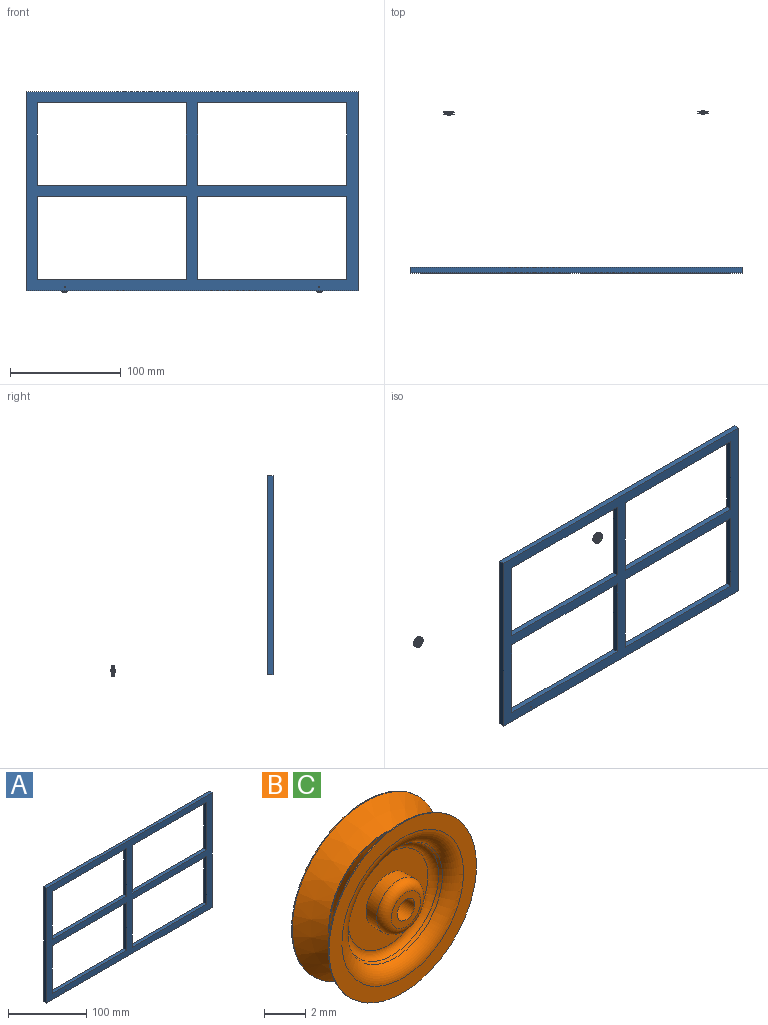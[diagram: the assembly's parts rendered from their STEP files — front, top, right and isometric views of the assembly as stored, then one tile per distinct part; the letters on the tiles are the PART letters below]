
ASSEMBLY  parts=3 mates=2
PART A: 24 faces, bbox 300x5x180 mm
  f0: plane 135x5mm, normal (0,0,-1), area 675mm2, adj f13,f14,f15,f16
  f1: plane 75x5mm, normal (-1,0,0), area 375mm2, adj f6,f14,f15,f21
  f2: plane 135x5mm, normal (0,0,1), area 675mm2, adj f3,f14,f15,f19
  f3: plane 75x5mm, normal (1,0,0), area 375mm2, adj f2,f14,f15,f18
  f4: plane 135x5mm, normal (0,0,-1), area 675mm2, adj f5,f14,f15,f23
  f5: plane 75x5mm, normal (-1,0,0), area 375mm2, adj f4,f14,f15,f22
  f6: plane 135x5mm, normal (0,0,1), area 675mm2, adj f1,f14,f15,f20
  f7: plane 180x5mm, normal (-1,0,0), area 900mm2, adj f8,f12,f14,f15
  f8: plane 300x5mm, normal (0,0,-1), area 1500mm2, adj f7,f9,f14,f15
  f9: plane 180x5mm, normal (1,0,0), area 900mm2, adj f8,f12,f14,f15
  f10: cylinder r=0.6mm len=5mm, axis (0,1,0), area 18.8mm2, adj f14,f15
  f11: cylinder r=0.6mm len=5mm, axis (0,1,0), area 18.8mm2, adj f14,f15
  f12: plane 300x5mm, normal (0,0,1), area 1500mm2, adj f7,f9,f14,f15
  f13: plane 75x5mm, normal (1,0,0), area 375mm2, adj f0,f14,f15,f17
  f14: plane 300x180mm, normal (0,-1,0), area 13497.7mm2, adj f0,f1,f2,f3,f4,f5,f6,f7
  f15: plane 300x180mm, normal (0,1,0), area 13497.7mm2, adj f0,f1,f2,f3,f4,f5,f6,f7
  f16: plane 75x5mm, normal (-1,0,0), area 375mm2, adj f0,f14,f15,f17
  f17: plane 135x5mm, normal (0,0,1), area 675mm2, adj f13,f14,f15,f16
  f18: plane 135x5mm, normal (0,0,-1), area 675mm2, adj f3,f14,f15,f19
  f19: plane 75x5mm, normal (-1,0,0), area 375mm2, adj f2,f14,f15,f18
  f20: plane 75x5mm, normal (1,0,0), area 375mm2, adj f6,f14,f15,f21
  f21: plane 135x5mm, normal (0,0,-1), area 675mm2, adj f1,f14,f15,f20
  f22: plane 135x5mm, normal (0,0,1), area 675mm2, adj f5,f14,f15,f23
  f23: plane 75x5mm, normal (1,0,0), area 375mm2, adj f4,f14,f15,f22
PART B: 25 faces, bbox 10.5x3x10.5 mm
  f0: cone r=5.03mm half-angle=47.2deg, axis (0,-1,0), area 48.6mm2, adj f1,f17
  f1: cylinder r=5.03mm len=10.07mm, axis (0,-1,0), area 1.6mm2, adj f0,f2
  f2: plane 10.07x10.07mm, normal (0,-1,0), area 25.4mm2, adj f1,f18
  f3: cone r=3.53mm half-angle=26.6deg, axis (0,-1,0), area 3.9mm2, adj f18,f19
  f4: plane 5.45x5.45mm, normal (0,-1,0), area 16.2mm2, adj f5,f19
  f5: cylinder r=1.5mm len=3mm, axis (0,-1,0), area 6.8mm2, adj f4,f20
  f6: plane 2x2mm, normal (0,-1,0), area 2mm2, adj f7,f20
  f7: cylinder r=0.6mm len=3mm, axis (0,-1,0), area 11.3mm2, adj f6,f8
  f8: plane 2x2mm, normal (0,1,0), area 2mm2, adj f7,f21
  f9: cylinder r=1.5mm len=3mm, axis (0,-1,0), area 2.1mm2, adj f21,f22
  f10: plane 5.45x5.45mm, normal (0,1,0), area 10.7mm2, adj f22,f23
  f11: cone r=3.53mm half-angle=26.6deg, axis (0,1,0), area 3.9mm2, adj f23,f24
  f12: plane 10.07x10.07mm, normal (0,1,0), area 25.4mm2, adj f13,f24
  f13: cylinder r=5.03mm len=10.07mm, axis (0,-1,0), area 1.6mm2, adj f12,f14
  f14: cone r=5.03mm half-angle=47.2deg, axis (0,1,0), area 48.6mm2, adj f13,f15
  f15: plane 7.48x7.48mm, normal (0,-1,0), area 1.4mm2, adj f14,f16
  f16: cylinder r=3.68mm len=7.36mm, axis (0,-1,0), area 1.4mm2, adj f15,f17
  f17: plane 7.48x7.48mm, normal (0,1,0), area 1.4mm2, adj f0,f16
  f18: torus R=4.15mm, axis (0,1,0), area 25.4mm2, adj f2,f3
  f19: torus R=2.72mm, axis (0,1,0), area 10.3mm2, adj f3,f4
  f20: torus R=1mm, axis (0,1,0), area 6.5mm2, adj f5,f6
  f21: torus R=1mm, axis (0,1,0), area 6.5mm2, adj f8,f9
  f22: torus R=2mm, axis (0,1,0), area 8.3mm2, adj f9,f10
  f23: torus R=2.72mm, axis (0,1,0), area 10.3mm2, adj f10,f11
  f24: torus R=4.15mm, axis (0,1,0), area 25.4mm2, adj f11,f12
PART C: same geometry as B
PLACE A t=(-22.6,-194.72,-10.81)mm
PLACE B t=(-137.6,-24.19,-13.43)mm
PLACE C t=(92.4,-23.41,-13.43)mm
MATE cylindrical B.f0 <-> A.f11  axis (0,-1,0) through (-137.6,-56.92,-97.31)mm
MATE cylindrical C.f0 <-> A.f10  axis (0,1,0) through (92.4,-53.14,-97.31)mm
